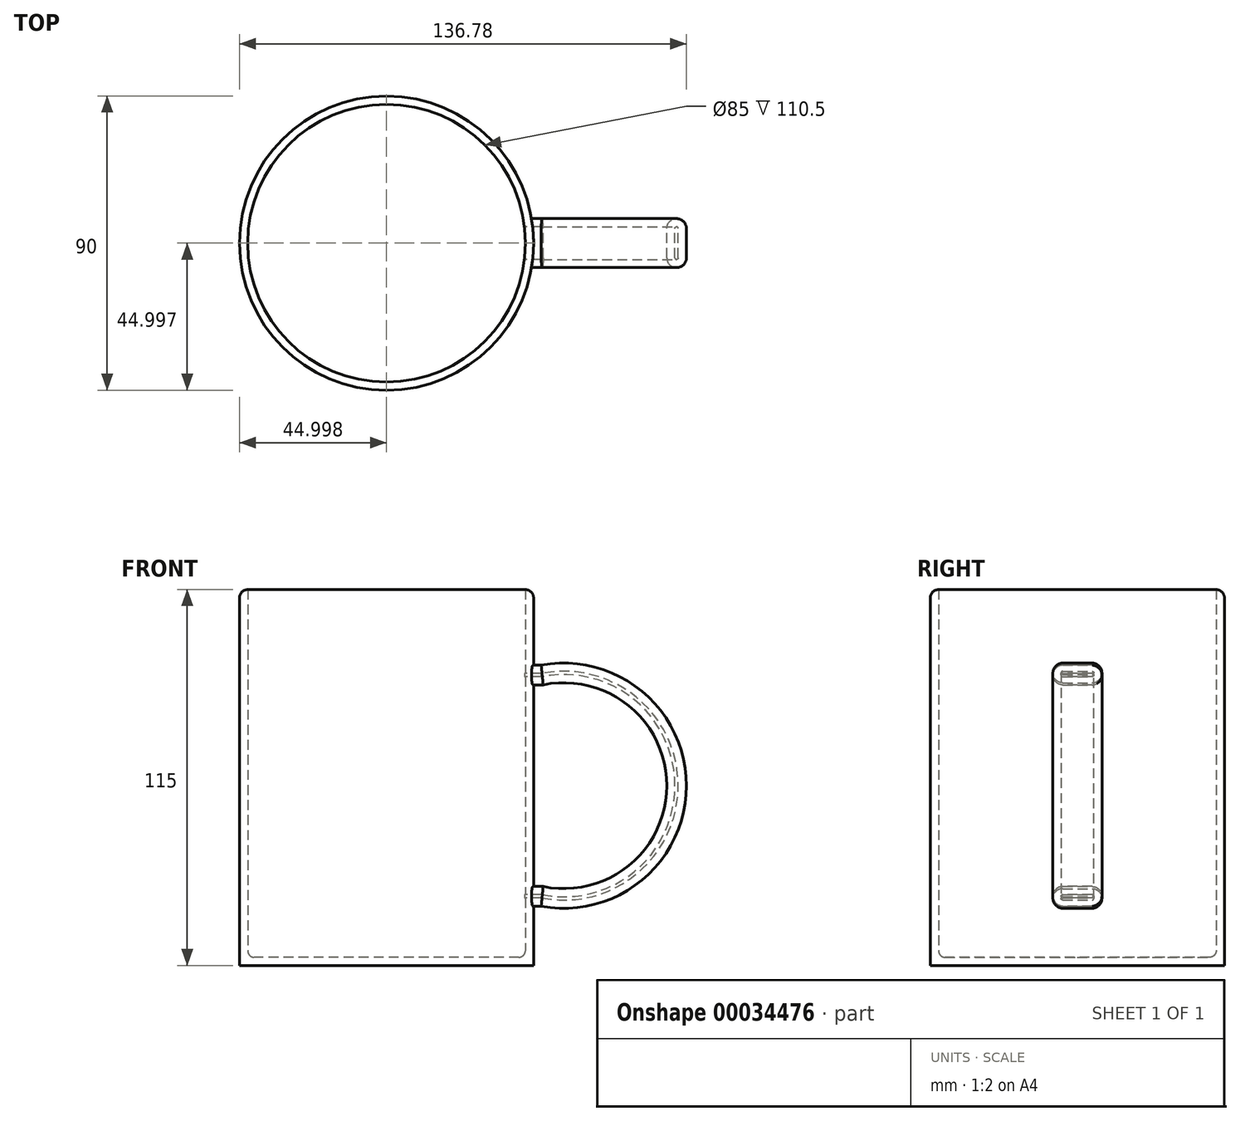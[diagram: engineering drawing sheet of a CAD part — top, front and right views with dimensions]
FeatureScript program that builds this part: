
annotation { "Feature Type Name" : "Feature", "Feature Type Description" : "" }
export const myFeature = defineFeature(function(context is Context, id is Id, definition is map)
    precondition{}
    {
        {
            var Q0;
            Q0=qCreatedBy(makeId("Front.planeOp"),FACE);
            var sketch = newSketch(context, id + "F0", { "sketchPlane" : qUnion([Q0])});
            skArc(sketch, "E0", {"start": v(-6.93, -36.85) * mm, "mid": v(37.5, 0) * mm, "end": v(-6.93, 36.85) * mm});
            skArc(sketch, "E1", {"start": v(-16.05, -31.1) * mm, "mid": v(35, 0) * mm, "end": v(-16.05, 31.1) * mm});
            skLineSegment(sketch, "E2.bottom", {"start": v(-6.93, 36.85) * mm, "end": v(-16.05, 36.85) * mm});
            skLineSegment(sketch, "E2.top", {"start": v(-6.93, -36.85) * mm, "end": v(-16.05, -36.85) * mm});
            skLineSegment(sketch, "E2.right", {"start": v(-16.05, 36.85) * mm, "end": v(-16.05, -36.85) * mm});
            skSolve(sketch);
        }
        {
            var Q0;
            Q0 = qSketchRegion(id + "F0", true);
            extrude(context, id + "F1", {"entities" : qUnion([Q0]), "depth" : 15 * mm});
        }
        {
            var Q0;
            Q0=makeQuery(id+"F1.opExtrude","CAP_FACE",FACE,{"disambiguationData":[OSD([sQuery(id+"F0.wireOp",EDGE,"E0"),sQuery(id+"F0.wireOp",EDGE,"E2.bottom"),sQuery(id+"F0.wireOp",EDGE,"E2.top"),sQuery(id+"F0.wireOp",EDGE,"E2.right")])],"isStart":false});
            var Q1;
            Q1=makeQuery(id+"F1.opExtrude","CAP_FACE",FACE,{"disambiguationData":[OSD([sQuery(id+"F0.wireOp",EDGE,"E0"),sQuery(id+"F0.wireOp",EDGE,"E2.bottom"),sQuery(id+"F0.wireOp",EDGE,"E2.top"),sQuery(id+"F0.wireOp",EDGE,"E2.right")])],"isStart":true});
            shell(context, id + "F2", {"entities" : qUnion([Q0, Q1]), "thickness" : 6 * mm});
        }
        {
            var Q0;
            {var subQ0=sQuery(id+"F0.wireOp",EDGE,"E2.bottom");Q0=makeQuery(id+"F2.opShell","OFFSET_EDGE",EDGE,{"disambiguationData":[OSD([subQ0]),TDD([makeQuery(id+"F1.opExtrude","CAP_EDGE",EDGE,{"disambiguationData":[OSD([subQ0])],"isStart":false})])]});}
            var Q1;
            {var subQ0=sQuery(id+"F0.wireOp",EDGE,"E0");Q1=makeQuery(id+"F2.opShell","OFFSET_EDGE",EDGE,{"disambiguationData":[OSD([subQ0]),TDD([makeQuery(id+"F1.opExtrude","CAP_EDGE",EDGE,{"disambiguationData":[OSD([subQ0])],"isStart":false})])]});}
            var Q2;
            {var subQ0=sQuery(id+"F0.wireOp",EDGE,"E2.top");Q2=makeQuery(id+"F2.opShell","OFFSET_EDGE",EDGE,{"disambiguationData":[OSD([subQ0]),TDD([makeQuery(id+"F1.opExtrude","CAP_EDGE",EDGE,{"disambiguationData":[OSD([subQ0])],"isStart":false})])]});}
            fillet(context, id + "F3", {"entities" : qUnion([Q0, Q1, Q2]), "radius" : 3 * mm, "tangentPropagation" : true, "allowEdgeOverflow" : false});
        }
        {
            var Q0;
            Q0=makeQuery(id+"F1.opExtrude","CAP_EDGE",EDGE,{"disambiguationData":[OSD([sQuery(id+"F0.wireOp",EDGE,"E2.bottom")])],"isStart":false});
            var Q1;
            Q1=makeQuery(id+"F1.opExtrude","CAP_EDGE",EDGE,{"disambiguationData":[OSD([sQuery(id+"F0.wireOp",EDGE,"E0")])],"isStart":false});
            var Q2;
            Q2=makeQuery(id+"F1.opExtrude","CAP_EDGE",EDGE,{"disambiguationData":[OSD([sQuery(id+"F0.wireOp",EDGE,"E2.top")])],"isStart":false});
            fillet(context, id + "F4", {"entities" : qUnion([Q0, Q1, Q2]), "radius" : 3 * mm, "tangentPropagation" : true, "allowEdgeOverflow" : false});
        }
        {
            var Q0;
            Q0=qCreatedBy(makeId("Top.planeOp"),FACE);
            var sketch = newSketch(context, id + "F5", { "sketchPlane" : qUnion([Q0])});
            skCircle(sketch, "E3", {"center": v(-54.28, -7.51) * mm, "radius": 45 * mm});
            skSolve(sketch);
        }
        {
            var Q0;
            Q0=makeQuery(id+"F5.imprint","IMPRINT",FACE,{"disambiguationData":[TD([[makeQuery(id+"F5.imprint","IMPRINT",EDGE,{"derivedFrom":sQuery(id+"F5.wireOp",EDGE,"E3")}),1.0]])]});
            extrude(context, id + "F6", {"entities" : qUnion([Q0]), "operationType" : NewBodyOperationType.ADD, "depth" : 60 * mm, "hasSecondDirection" : true, "secondDirectionOppositeDirection" : true, "secondDirectionDepth" : 55 * mm});
        }
        {
            var Q0;
            {var subQ0=sQuery(id+"F0.wireOp",EDGE,"E2.top");Q0=makeQuery(id+"F2.opShell","OFFSET_EDGE",EDGE,{"disambiguationData":[OSD([subQ0]),TDD([makeQuery(id+"F1.opExtrude","CAP_EDGE",EDGE,{"disambiguationData":[OSD([subQ0])],"isStart":true})])]});}
            var Q1;
            {var subQ0=sQuery(id+"F0.wireOp",EDGE,"E0");Q1=makeQuery(id+"F2.opShell","OFFSET_EDGE",EDGE,{"disambiguationData":[OSD([subQ0]),TDD([makeQuery(id+"F1.opExtrude","CAP_EDGE",EDGE,{"disambiguationData":[OSD([subQ0])],"isStart":true})])]});}
            var Q2;
            {var subQ0=sQuery(id+"F0.wireOp",EDGE,"E2.bottom");Q2=makeQuery(id+"F2.opShell","OFFSET_EDGE",EDGE,{"disambiguationData":[OSD([subQ0]),TDD([makeQuery(id+"F1.opExtrude","CAP_EDGE",EDGE,{"disambiguationData":[OSD([subQ0])],"isStart":true})])]});}
            var Q3;
            Q3=makeQuery(id+"F1.opExtrude","CAP_EDGE",EDGE,{"disambiguationData":[OSD([sQuery(id+"F0.wireOp",EDGE,"E2.top")])],"isStart":true});
            var Q4;
            Q4=makeQuery(id+"F1.opExtrude","CAP_EDGE",EDGE,{"disambiguationData":[OSD([sQuery(id+"F0.wireOp",EDGE,"E0")])],"isStart":true});
            var Q5;
            Q5=makeQuery(id+"F1.opExtrude","CAP_EDGE",EDGE,{"disambiguationData":[OSD([sQuery(id+"F0.wireOp",EDGE,"E2.bottom")])],"isStart":true});
            fillet(context, id + "F7", {"entities" : qUnion([Q0, Q1, Q2, Q3, Q4, Q5]), "radius" : 3 * mm, "tangentPropagation" : true, "allowEdgeOverflow" : false});
        }
        {
            var Q0;
            Q0=makeQuery(id+"F6.opExtrude","CAP_FACE",FACE,{"disambiguationData":[OSD([sQuery(id+"F5.wireOp",EDGE,"E3")])],"isStart":false});
            shell(context, id + "F8", {"entities" : qUnion([Q0]), "thickness" : 2.5 * mm});
        }
        {
            var Q0;
            {var subQ0=sQuery(id+"F5.wireOp",EDGE,"E3");Q0=makeQuery(id+"F8.opShell","OFFSET_EDGE",EDGE,{"disambiguationData":[OSD([subQ0]),TDD([makeQuery(id+"F6.opExtrude","CAP_EDGE",EDGE,{"disambiguationData":[OSD([subQ0])],"isStart":true})])]});}
            fillet(context, id + "F9", {"entities" : qUnion([Q0]), "radius" : 2 * mm, "tangentPropagation" : true, "allowEdgeOverflow" : false});
        }
        {
            var Q0;
            Q0=makeQuery(id+"F6.opExtrude","CAP_EDGE",EDGE,{"disambiguationData":[OSD([sQuery(id+"F5.wireOp",EDGE,"E3")])],"isStart":false});
            fillet(context, id + "F10", {"entities" : qUnion([Q0]), "radius" : 2.5 * mm, "tangentPropagation" : true, "allowEdgeOverflow" : false});
        }
    });
